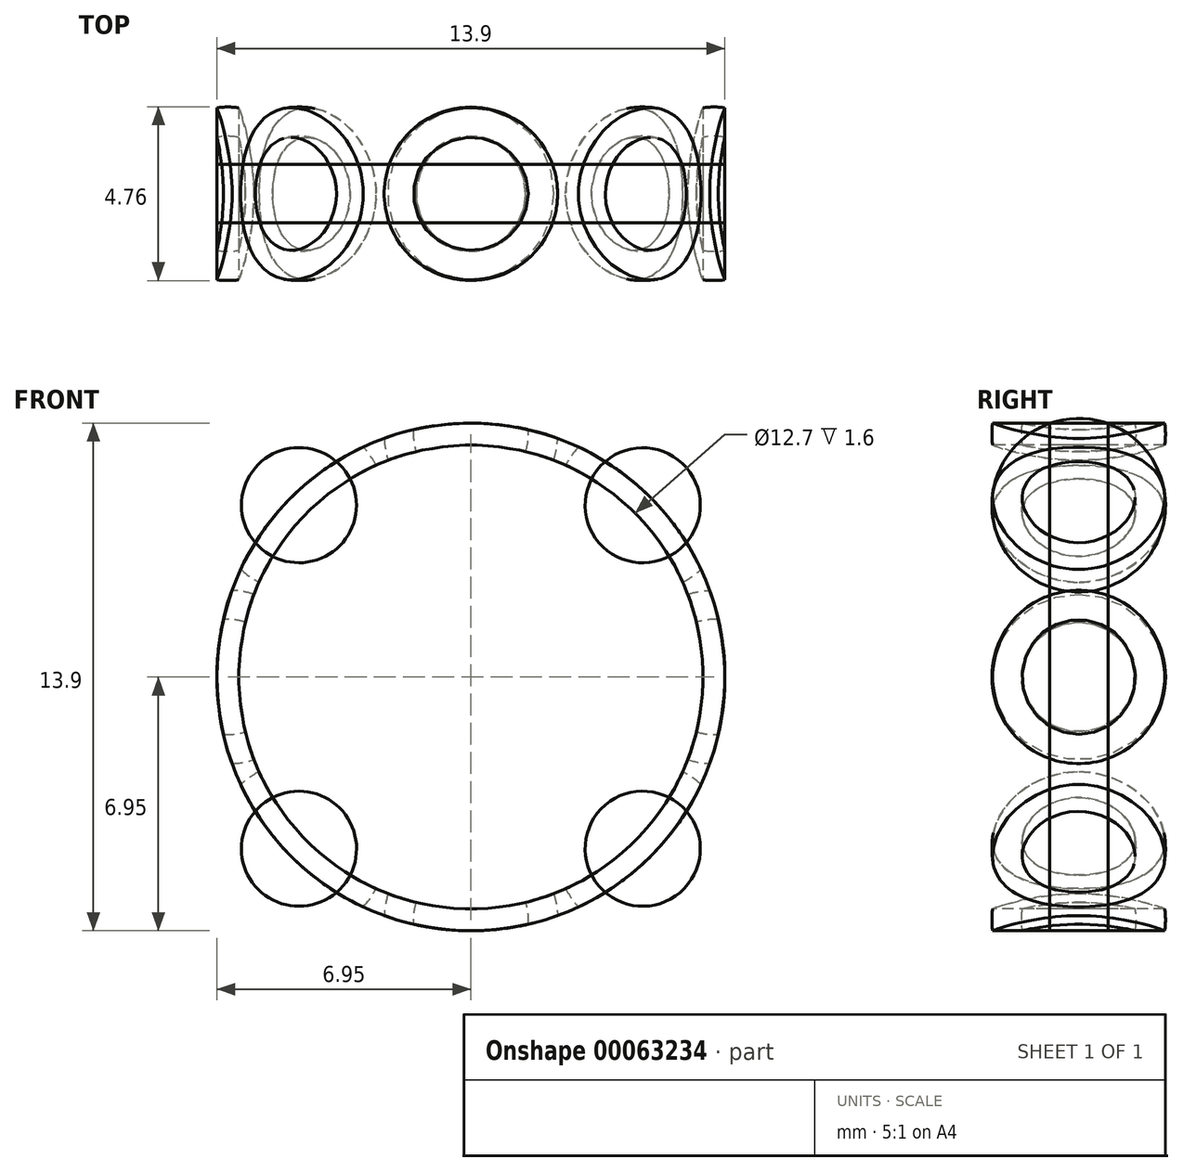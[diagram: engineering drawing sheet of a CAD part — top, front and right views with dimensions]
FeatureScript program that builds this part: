
annotation { "Feature Type Name" : "Feature", "Feature Type Description" : "" }
export const myFeature = defineFeature(function(context is Context, id is Id, definition is map)
    precondition{}
    {
        {
            var Q0;
            Q0=qCreatedBy(makeId("Right.planeOp"),FACE);
            var sketch = newSketch(context, id + "F0", { "sketchPlane" : qUnion([Q0])});
            skLineSegment(sketch, "E0", {"start": v(0, 9.5) * mm, "end": v(3, 9.5) * mm});
            skLineSegment(sketch, "E1", {"start": v(3, 7.9) * mm, "end": v(3, 9.5) * mm});
            skLineSegment(sketch, "E2", {"start": v(3, 7.9) * mm, "end": v(0.96, 7.9) * mm});
            skLineSegment(sketch, "E3", {"start": v(0.89, 5.35) * mm, "end": v(3, 5.35) * mm});
            skLineSegment(sketch, "E4", {"start": v(3, 5.35) * mm, "end": v(3, 3) * mm});
            skLineSegment(sketch, "E5", {"start": v(3, 3) * mm, "end": v(0, 3) * mm});
            skLineSegment(sketch, "E6.MirrorCS", {"start": v(0, 9.5) * mm, "end": v(-3, 9.5) * mm});
            skLineSegment(sketch, "E7.MirrorCS", {"start": v(-3, 3) * mm, "end": v(0, 3) * mm});
            skLineSegment(sketch, "E8.MirrorCS", {"start": v(-3, 5.35) * mm, "end": v(-3, 3) * mm});
            skLineSegment(sketch, "E9.MirrorCS", {"start": v(-0.89, 5.35) * mm, "end": v(-3, 5.35) * mm});
            skLineSegment(sketch, "E10.MirrorCS", {"start": v(-3, 7.9) * mm, "end": v(-3, 9.5) * mm});
            skLineSegment(sketch, "E11.MirrorCS", {"start": v(-3, 7.9) * mm, "end": v(-0.96, 7.9) * mm});
            skLineSegment(sketch, "E12", {"start": v(-5.39, 0) * mm, "end": v(7.08, 0) * mm});
            skPoint(sketch, "E13", {"position": v(0, 6.65) * mm});
            skArc(sketch, "E14", {"start": v(-0.89, 5.35) * mm, "mid": v(0, 5.08) * mm, "end": v(0.89, 5.35) * mm});
            skArc(sketch, "E15.trimOffspring", {"start": v(0.96, 7.9) * mm, "mid": v(0, 8.23) * mm, "end": v(-0.96, 7.9) * mm});
            skSolve(sketch);
        }
        {
            var Q0;
            Q0=makeQuery(id+"F0.imprint","IMPRINT",FACE,{"disambiguationData":[TD([[makeQuery(id+"F0.imprint","IMPRINT",EDGE,{"derivedFrom":sQuery(id+"F0.wireOp",EDGE,"E0")}),-1.0]])]});
            var Q1;
            Q1=sQuery(id+"F0.wireOp",EDGE,"E12");
            revolve(context, id + "F1", {"entities" : qUnion([Q0]), "axis" : qUnion([Q1]), "revolveType" : RevolveType.FULL});
        }
        {
            var Q0;
            Q0=makeQuery(id+"F0.imprint","IMPRINT",FACE,{"disambiguationData":[TD([[makeQuery(id+"F0.imprint","IMPRINT",EDGE,{"derivedFrom":sQuery(id+"F0.wireOp",EDGE,"E3")}),-1.0]])]});
            var Q1;
            Q1=sQuery(id+"F0.wireOp",EDGE,"E12");
            revolve(context, id + "F2", {"entities" : qUnion([Q0]), "axis" : qUnion([Q1]), "revolveType" : RevolveType.FULL});
        }
        {
            var Q0;
            Q0=makeQuery(id+"F1.opRevolve","SWEPT_EDGE",EDGE,{"disambiguationData":[OSD([sQuery(id+"F0.wireOp",EDGE,"E6.MirrorCS"),sQuery(id+"F0.wireOp",EDGE,"E10.MirrorCS")])]});
            var Q1;
            Q1=makeQuery(id+"F1.opRevolve","SWEPT_EDGE",EDGE,{"disambiguationData":[OSD([sQuery(id+"F0.wireOp",EDGE,"E0"),sQuery(id+"F0.wireOp",EDGE,"E1")])]});
            var Q2;
            Q2=makeQuery(id+"F2.opRevolve","SWEPT_EDGE",EDGE,{"disambiguationData":[OSD([sQuery(id+"F0.wireOp",EDGE,"E7.MirrorCS"),sQuery(id+"F0.wireOp",EDGE,"E8.MirrorCS")])]});
            var Q3;
            Q3=makeQuery(id+"F2.opRevolve","SWEPT_EDGE",EDGE,{"disambiguationData":[OSD([sQuery(id+"F0.wireOp",EDGE,"E4"),sQuery(id+"F0.wireOp",EDGE,"E5")])]});
            fillet(context, id + "F3", {"entities" : qUnion([Q0, Q1, Q2, Q3]), "radius" : 0.3 * mm, "tangentPropagation" : true, "allowEdgeOverflow" : false});
        }
        {
            var Q0;
            Q0=qCreatedBy(makeId("Front.planeOp"),FACE);
            var sketch = newSketch(context, id + "F4", { "sketchPlane" : qUnion([Q0])});
            skArc(sketch, "E16", {"start": v(0, 5.08) * mm, "mid": v(1.57, 6.65) * mm, "end": v(0, 8.22) * mm});
            skLineSegment(sketch, "E17", {"start": v(0, 8.22) * mm, "end": v(0, 5.08) * mm});
            skSolve(sketch);
        }
        {
            var Q0;
            Q0 = qSketchRegion(id + "F4", true);
            var Q1;
            Q1=makeQuery(id+"F4.imprint","IMPRINT",FACE,{"disambiguationData":[TD([[makeQuery(id+"F4.imprint","IMPRINT",EDGE,{"derivedFrom":sQuery(id+"F4.wireOp",EDGE,"E16")}),1.0]])]});
            var Q2;
            Q2=sQuery(id+"F4.wireOp",EDGE,"E17");
            revolve(context, id + "F5", {"entities" : qUnion([Q0, Q1]), "axis" : qUnion([Q2]), "revolveType" : RevolveType.ONE_DIRECTION, "angle" : 360 * degree});
        }
        {
            var Q0;
            Q0=qCreatedBy(makeId("Right.planeOp"),FACE);
            var sketch = newSketch(context, id + "F6", { "sketchPlane" : qUnion([Q0])});
            skPoint(sketch, "E18.0", {"position": v(0, 6.65) * mm});
            skLineSegment(sketch, "E19.bottom", {"start": v(-0.8, 6.95) * mm, "end": v(0.8, 6.95) * mm});
            skLineSegment(sketch, "E19.top", {"start": v(-0.8, 6.35) * mm, "end": v(0.8, 6.35) * mm});
            skLineSegment(sketch, "E19.left", {"start": v(-0.8, 6.95) * mm, "end": v(-0.8, 6.35) * mm});
            skLineSegment(sketch, "E19.right", {"start": v(0.8, 6.95) * mm, "end": v(0.8, 6.35) * mm});
            skSolve(sketch);
        }
        {
            var Q0;
            Q0=makeQuery(id+"F5.opRevolve","SWEPT_BODY",BODY,{"disambiguationData":[OSD([sQuery(id+"F4.wireOp",EDGE,"E16"),sQuery(id+"F4.wireOp",EDGE,"E17")])]});
            var Q1;
            Q1=sQuery(id+"F0.wireOp",EDGE,"E12");
            circularPattern(context, id + "F7", {"entities" : qUnion([Q0]), "axis" : qUnion([Q1]), "angle" : 45 * degree, "instanceCount" : 8});
        }
        {
            var Q0;
            Q0=makeQuery(id+"F6.imprint","IMPRINT",FACE,{"disambiguationData":[TD([[makeQuery(id+"F6.imprint","IMPRINT",EDGE,{"derivedFrom":sQuery(id+"F6.wireOp",EDGE,"E19.bottom")}),-1.0]])]});
            var Q1;
            Q1=sQuery(id+"F0.wireOp",EDGE,"E12");
            revolve(context, id + "F8", {"entities" : qUnion([Q0]), "axis" : qUnion([Q1]), "revolveType" : RevolveType.FULL});
        }
        {
            var Q0;
            Q0=qCreatedBy(makeId("Right.planeOp"),FACE);
            var sketch = newSketch(context, id + "F9", { "sketchPlane" : qUnion([Q0])});
            skArc(sketch, "E20", {"start": v(-2.36, 6.95) * mm, "mid": v(-2.37, 6.65) * mm, "end": v(-2.36, 6.35) * mm});
            skLineSegment(sketch, "E21.rect.bottom", {"start": v(-2.36, 6.35) * mm, "end": v(2.36, 6.35) * mm});
            skLineSegment(sketch, "E21.rect.top", {"start": v(-2.36, 6.95) * mm, "end": v(2.36, 6.95) * mm});
            skLineSegment(sketch, "E22.0", {"start": v(-0.8, 6.95) * mm, "end": v(0.8, 6.95) * mm});
            skArc(sketch, "E23.trimOffspring", {"start": v(2.36, 6.35) * mm, "mid": v(2.38, 6.65) * mm, "end": v(2.36, 6.95) * mm});
            skSolve(sketch);
        }
        {
            var Q0;
            Q0=qCreatedBy(makeId("Front.planeOp"),FACE);
            var sketch = newSketch(context, id + "F10", { "sketchPlane" : qUnion([Q0])});
            skLineSegment(sketch, "E24.0", {"start": v(0, 9.03) * mm, "end": v(0, 4.28) * mm});
            skArc(sketch, "E25.0", {"start": v(0, 4.28) * mm, "mid": v(2.38, 6.65) * mm, "end": v(0, 9.03) * mm});
            skPoint(sketch, "E26.orphan", {"position": v(0, 5.08) * mm});
            skPoint(sketch, "E27.orphan", {"position": v(0, 8.22) * mm});
            skSolve(sketch);
        }
        {
            var Q0;
            Q0=makeQuery(id+"F10.imprint","IMPRINT",FACE,{"disambiguationData":[TD([[makeQuery(id+"F10.imprint","IMPRINT",EDGE,{"derivedFrom":sQuery(id+"F10.wireOp",EDGE,"E24.0")}),1.0]])]});
            var Q1;
            Q1=sQuery(id+"F10.wireOp",EDGE,"E24.0");
            revolve(context, id + "F11", {"entities" : qUnion([Q0]), "axis" : qUnion([Q1]), "revolveType" : RevolveType.FULL});
        }
        {
            var Q0;
            Q0=makeQuery(id+"F11.opRevolve","SWEPT_BODY",BODY,{"disambiguationData":[OSD([sQuery(id+"F10.wireOp",EDGE,"E24.0"),sQuery(id+"F10.wireOp",EDGE,"E25.0")])]});
            var Q1;
            Q1=sQuery(id+"F0.wireOp",EDGE,"E12");
            circularPattern(context, id + "F12", {"entities" : qUnion([Q0]), "axis" : qUnion([Q1]), "angle" : 45 * degree, "instanceCount" : 8});
        }
        {
            var Q0;
            Q0 = qSketchRegion(id + "F9", true);
            var Q1;
            Q1=sQuery(id+"F0.wireOp",EDGE,"E12");
            revolve(context, id + "F13", {"operationType" : NewBodyOperationType.INTERSECT, "entities" : qUnion([Q0]), "axis" : qUnion([Q1]), "revolveType" : RevolveType.FULL});
        }
        {
            var Q0;
            Q0=makeQuery(id+"F5.opRevolve","SWEPT_BODY",BODY,{"disambiguationData":[OSD([sQuery(id+"F4.wireOp",EDGE,"E16"),sQuery(id+"F4.wireOp",EDGE,"E17")])]});
            var Q1;
            Q1=makeQuery(id+"F7.opPattern","COPY",BODY,{"derivedFrom":makeQuery(id+"F5.opRevolve","SWEPT_BODY",BODY,{"disambiguationData":[OSD([sQuery(id+"F4.wireOp",EDGE,"E16"),sQuery(id+"F4.wireOp",EDGE,"E17")])]}),"instanceName":"1"});
            var Q2;
            Q2=makeQuery(id+"F7.opPattern","COPY",BODY,{"derivedFrom":makeQuery(id+"F5.opRevolve","SWEPT_BODY",BODY,{"disambiguationData":[OSD([sQuery(id+"F4.wireOp",EDGE,"E16"),sQuery(id+"F4.wireOp",EDGE,"E17")])]}),"instanceName":"2"});
            var Q3;
            Q3=makeQuery(id+"F7.opPattern","COPY",BODY,{"derivedFrom":makeQuery(id+"F5.opRevolve","SWEPT_BODY",BODY,{"disambiguationData":[OSD([sQuery(id+"F4.wireOp",EDGE,"E16"),sQuery(id+"F4.wireOp",EDGE,"E17")])]}),"instanceName":"3"});
            var Q4;
            Q4=makeQuery(id+"F7.opPattern","COPY",BODY,{"derivedFrom":makeQuery(id+"F5.opRevolve","SWEPT_BODY",BODY,{"disambiguationData":[OSD([sQuery(id+"F4.wireOp",EDGE,"E16"),sQuery(id+"F4.wireOp",EDGE,"E17")])]}),"instanceName":"4"});
            var Q5;
            Q5=makeQuery(id+"F7.opPattern","COPY",BODY,{"derivedFrom":makeQuery(id+"F5.opRevolve","SWEPT_BODY",BODY,{"disambiguationData":[OSD([sQuery(id+"F4.wireOp",EDGE,"E16"),sQuery(id+"F4.wireOp",EDGE,"E17")])]}),"instanceName":"5"});
            var Q6;
            Q6=makeQuery(id+"F7.opPattern","COPY",BODY,{"derivedFrom":makeQuery(id+"F5.opRevolve","SWEPT_BODY",BODY,{"disambiguationData":[OSD([sQuery(id+"F4.wireOp",EDGE,"E16"),sQuery(id+"F4.wireOp",EDGE,"E17")])]}),"instanceName":"6"});
            var Q7;
            Q7=makeQuery(id+"F7.opPattern","COPY",BODY,{"derivedFrom":makeQuery(id+"F5.opRevolve","SWEPT_BODY",BODY,{"disambiguationData":[OSD([sQuery(id+"F4.wireOp",EDGE,"E16"),sQuery(id+"F4.wireOp",EDGE,"E17")])]}),"instanceName":"7"});
            var Q8;
            Q8=makeQuery(id+"F11.opRevolve","SWEPT_BODY",BODY,{"disambiguationData":[OSD([sQuery(id+"F10.wireOp",EDGE,"E24.0"),sQuery(id+"F10.wireOp",EDGE,"E25.0")])]});
            booleanBodies(context, id + "F14", {"operationType" : BooleanOperationType.SUBTRACTION, "tools" : qUnion([Q0, Q1, Q2, Q3, Q4, Q5, Q6, Q7]), "targets" : qUnion([Q8]), "keepTools" : true});
        }
    });
